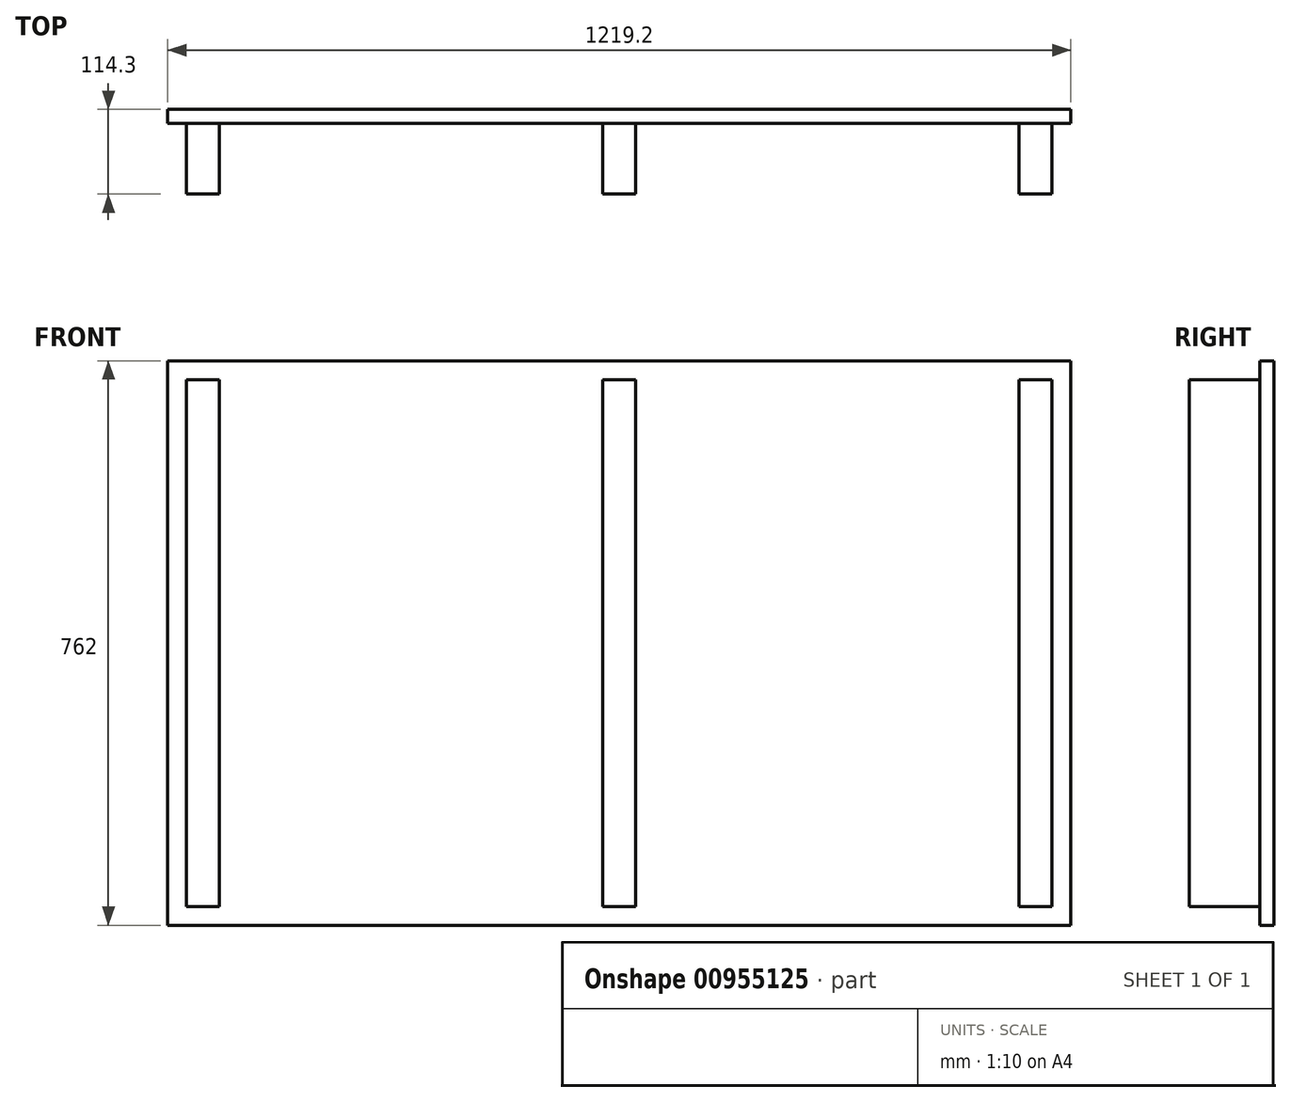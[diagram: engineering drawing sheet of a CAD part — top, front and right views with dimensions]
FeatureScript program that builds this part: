
annotation { "Feature Type Name" : "Feature", "Feature Type Description" : "" }
export const myFeature = defineFeature(function(context is Context, id is Id, definition is map)
    precondition{}
    {
        {
            var Q0;
            Q0=qCreatedBy(makeId("Front.planeOp"),FACE);
            var sketch = newSketch(context, id + "F0", { "sketchPlane" : qUnion([Q0])});
            skLineSegment(sketch, "E0.bottom", {"start": v(609.6, 381) * mm, "end": v(-609.6, 381) * mm});
            skLineSegment(sketch, "E0.top", {"start": v(609.6, -381) * mm, "end": v(-609.6, -381) * mm});
            skLineSegment(sketch, "E0.left", {"start": v(609.6, 381) * mm, "end": v(609.6, -381) * mm});
            skLineSegment(sketch, "E0.right", {"start": v(-609.6, 381) * mm, "end": v(-609.6, -381) * mm});
            skPoint(sketch, "E0.middle", {"position": v(0, 0) * mm});
            skLineSegment(sketch, "E1.bottom", {"start": v(-539.75, 355.6) * mm, "end": v(-584.2, 355.6) * mm});
            skLineSegment(sketch, "E1.top", {"start": v(-539.75, -355.6) * mm, "end": v(-584.2, -355.6) * mm});
            skLineSegment(sketch, "E1.left", {"start": v(-539.75, 355.6) * mm, "end": v(-539.75, -355.6) * mm});
            skLineSegment(sketch, "E1.right", {"start": v(-584.2, 355.6) * mm, "end": v(-584.2, -355.6) * mm});
            skPoint(sketch, "E1.middle", {"position": v(-561.98, 0) * mm});
            skLineSegment(sketch, "E2.bottom", {"start": v(22.22, 355.6) * mm, "end": v(-22.22, 355.6) * mm});
            skLineSegment(sketch, "E2.top", {"start": v(22.22, -355.6) * mm, "end": v(-22.22, -355.6) * mm});
            skLineSegment(sketch, "E2.left", {"start": v(22.23, 355.6) * mm, "end": v(22.23, -355.6) * mm});
            skLineSegment(sketch, "E2.right", {"start": v(-22.23, 355.6) * mm, "end": v(-22.23, -355.6) * mm});
            skLineSegment(sketch, "E3.bottom", {"start": v(584.2, 355.6) * mm, "end": v(539.75, 355.6) * mm});
            skLineSegment(sketch, "E3.top", {"start": v(584.2, -355.6) * mm, "end": v(539.75, -355.6) * mm});
            skLineSegment(sketch, "E3.left", {"start": v(584.2, 355.6) * mm, "end": v(584.2, -355.6) * mm});
            skLineSegment(sketch, "E3.right", {"start": v(539.75, 355.6) * mm, "end": v(539.75, -355.6) * mm});
            skPoint(sketch, "E3.middle", {"position": v(561.98, 0) * mm});
            skSolve(sketch);
        }
        {
            var Q0;
            Q0=makeQuery(id+"F0.imprint","IMPRINT",FACE,{"disambiguationData":[TD([[makeQuery(id+"F0.imprint","IMPRINT",EDGE,{"derivedFrom":sQuery(id+"F0.wireOp",EDGE,"E2.bottom")}),1.0]])]});
            var Q1;
            Q1=makeQuery(id+"F0.imprint","IMPRINT",FACE,{"disambiguationData":[TD([[makeQuery(id+"F0.imprint","IMPRINT",EDGE,{"derivedFrom":sQuery(id+"F0.wireOp",EDGE,"E1.bottom")}),1.0]])]});
            var Q2;
            Q2=makeQuery(id+"F0.imprint","IMPRINT",FACE,{"disambiguationData":[TD([[makeQuery(id+"F0.imprint","IMPRINT",EDGE,{"derivedFrom":sQuery(id+"F0.wireOp",EDGE,"E3.bottom")}),1.0]])]});
            extrude(context, id + "F1", {"entities" : qUnion([Q0, Q1, Q2]), "depth" : 95.25 * mm, "offsetDistance" : 25.4 * mm});
        }
        {
            var Q0;
            Q0=makeQuery(id+"F0.imprint","IMPRINT",FACE,{"disambiguationData":[TD([[makeQuery(id+"F0.imprint","IMPRINT",EDGE,{"derivedFrom":sQuery(id+"F0.wireOp",EDGE,"E0.bottom")}),1.0]])]});
            var Q1;
            Q1=makeQuery(id+"F0.imprint","IMPRINT",FACE,{"disambiguationData":[TD([[makeQuery(id+"F0.imprint","IMPRINT",EDGE,{"derivedFrom":sQuery(id+"F0.wireOp",EDGE,"E2.bottom")}),1.0]])]});
            var Q2;
            Q2=makeQuery(id+"F0.imprint","IMPRINT",FACE,{"disambiguationData":[TD([[makeQuery(id+"F0.imprint","IMPRINT",EDGE,{"derivedFrom":sQuery(id+"F0.wireOp",EDGE,"E1.bottom")}),1.0]])]});
            var Q3;
            Q3=makeQuery(id+"F0.imprint","IMPRINT",FACE,{"disambiguationData":[TD([[makeQuery(id+"F0.imprint","IMPRINT",EDGE,{"derivedFrom":sQuery(id+"F0.wireOp",EDGE,"E3.bottom")}),1.0]])]});
            extrude(context, id + "F2", {"entities" : qUnion([Q0, Q1, Q2, Q3]), "oppositeDirection" : true, "depth" : 19.05 * mm, "offsetDistance" : 25.4 * mm});
        }
    });
